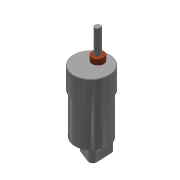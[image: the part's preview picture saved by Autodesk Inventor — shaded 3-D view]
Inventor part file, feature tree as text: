
AUTODESK INVENTOR PART (.ipt)
format: ipt  version: 2013 (Build 170138000, 138)  size: 249,856 bytes
history: native  units: in
note: dims shown in document units (in); Inventor stores cm internally (conversion verified against a paired STEP export)
features: extrude x4, sketch x4, fillet x2, other x1, imported_body x1
ambient origin geometry x8: Origin, YZ Plane, XZ Plane, XY Plane, X Axis, Y Axis, Z Axis, Center Point
bodies: Solid2 (feature_tree)
feature tree (12):
  other  "DC_MOTOR_2011"
  imported_body  "Base1"
  extrude  "Extrusion1"  Depth=0.5909in
  extrude  "Extrusion2"  Depth=0.4528in
  extrude  "Extrusion3"  Depth=0.1654in TaperAngle=0.0deg
  fillet  "Fillet1"  Radius=0.748in
  fillet  "Fillet2"  Radius=0.4331in
  extrude  "Extrusion4"  Depth=0.2165in
  sketch  "Sketch1"  dims[d0=0.315in d1=0.5909in]
  sketch  "Sketch2"  dims[d3=0.3436in d5=0.4528in]
  sketch  "Sketch3"  dims[d6=0.4528in d7=0.1654in d8=0.0in d9=0.748in d11=0.4331in]
  sketch  "Sketch4"  dims[d12=0.3661in d13=0.0in d14=0.2165in d16=0.0472in d17=0.0in d18=0.0197in d19=0.0787in d20=0.1181in d21=0.1181in d22=0.5906in d23=0.0in]
